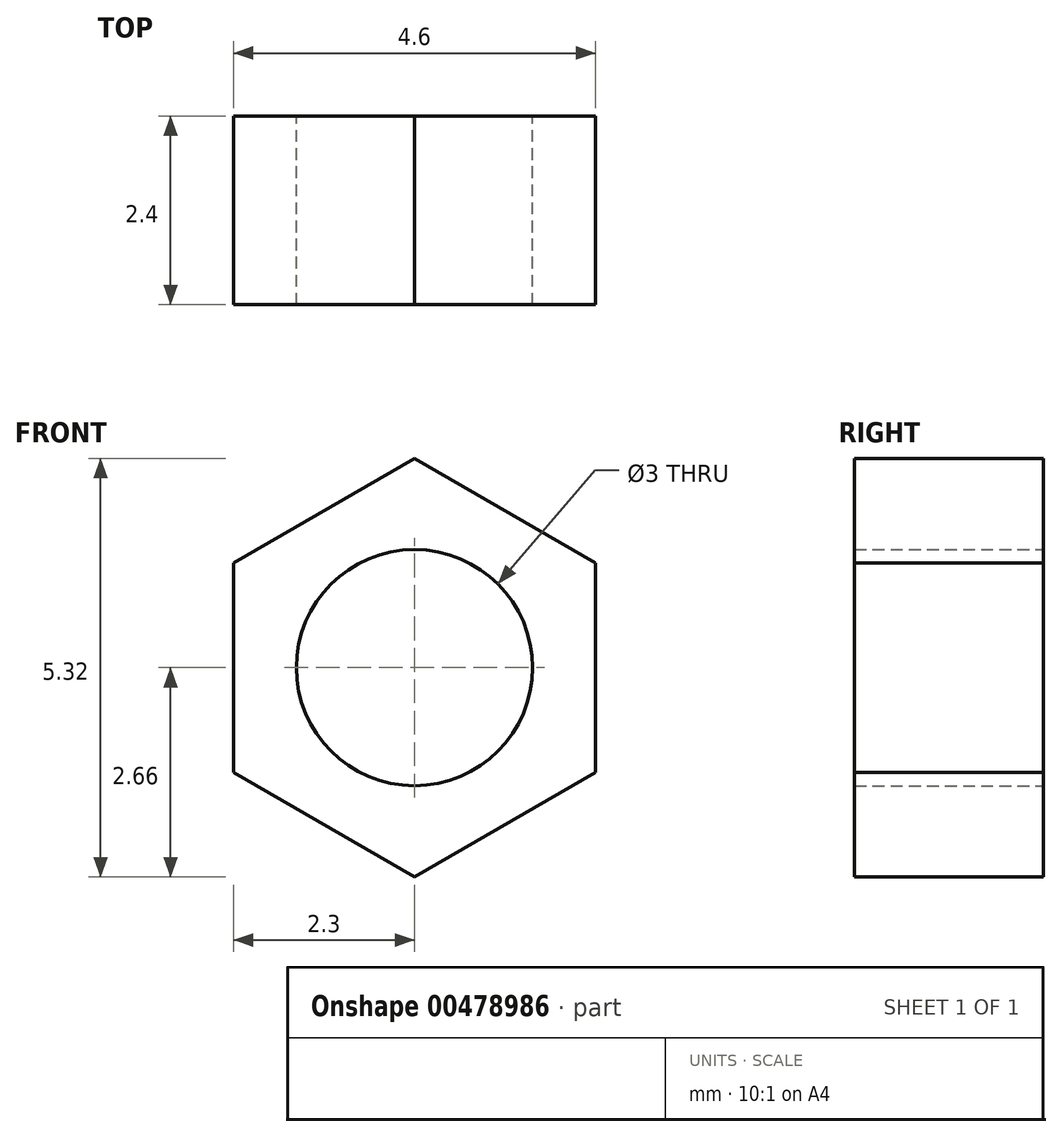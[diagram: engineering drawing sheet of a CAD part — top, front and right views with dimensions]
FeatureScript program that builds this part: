
annotation { "Feature Type Name" : "Feature", "Feature Type Description" : "" }
export const myFeature = defineFeature(function(context is Context, id is Id, definition is map)
    precondition{}
    {
        {
            var Q0;
            Q0=qCreatedBy(makeId("Front.planeOp"),FACE);
            var sketch = newSketch(context, id + "F0", { "sketchPlane" : qUnion([Q0])});
            skCircle(sketch, "E0", {"center": v(0, 0) * mm, "radius": 1.5 * mm});
            skCircle(sketch, "E1.cCircle", {"center": v(0, 0) * mm, "radius": 2.3 * mm, "construction": true});
            skLineSegment(sketch, "E1.0", {"start": v(2.3, 1.33) * mm, "end": v(2.3, -1.33) * mm});
            skLineSegment(sketch, "E1.1", {"start": v(2.3, -1.33) * mm, "end": v(0, -2.66) * mm});
            skLineSegment(sketch, "E1.2", {"start": v(0, -2.66) * mm, "end": v(-2.3, -1.33) * mm});
            skLineSegment(sketch, "E1.3", {"start": v(-2.3, -1.33) * mm, "end": v(-2.3, 1.33) * mm});
            skLineSegment(sketch, "E1.4", {"start": v(-2.3, 1.33) * mm, "end": v(0, 2.66) * mm});
            skLineSegment(sketch, "E1.5", {"start": v(0, 2.66) * mm, "end": v(2.3, 1.33) * mm});
            skPoint(sketch, "E1.0.midPoint", {"position": v(2.3, 0) * mm});
            skSolve(sketch);
        }
        {
            var Q0;
            Q0 = qSketchRegion(id + "F0", true);
            extrude(context, id + "F1", {"entities" : qUnion([Q0]), "depth" : 2.4 * mm});
        }
    });
